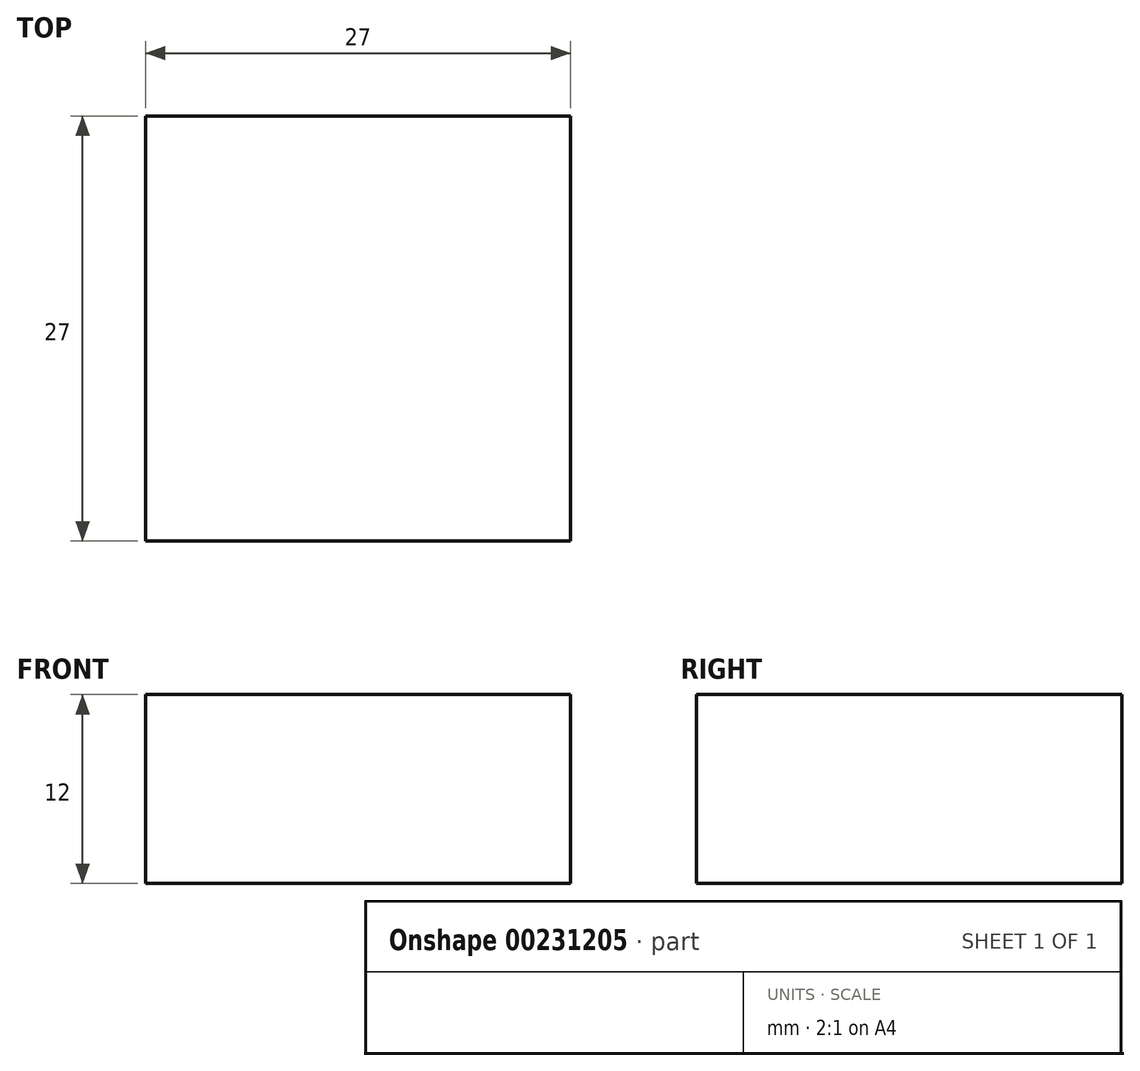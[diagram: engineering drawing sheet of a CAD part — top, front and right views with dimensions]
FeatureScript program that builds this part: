
annotation { "Feature Type Name" : "Feature", "Feature Type Description" : "" }
export const myFeature = defineFeature(function(context is Context, id is Id, definition is map)
    precondition{}
    {
        {
            assignVariable(context, id + "F0", {"name" : "foot_servo_width", "anyValue" : 12});
        }
        {
            var Q0;
            Q0=qCreatedBy(makeId("Top.planeOp"),FACE);
            var sketch = newSketch(context, id + "F1", { "sketchPlane" : qUnion([Q0])});
            skLineSegment(sketch, "E0.bottom", {"start": v(-35.31, -13.5) * mm, "end": v(-8.31, -13.5) * mm});
            skLineSegment(sketch, "E0.top", {"start": v(-35.31, 13.5) * mm, "end": v(-8.31, 13.5) * mm});
            skLineSegment(sketch, "E0.left", {"start": v(-35.31, -13.5) * mm, "end": v(-35.31, 13.5) * mm});
            skLineSegment(sketch, "E0.right", {"start": v(-8.31, -13.5) * mm, "end": v(-8.31, 13.5) * mm});
            skPoint(sketch, "E0.middle", {"position": v(-21.81, 0) * mm});
            skSolve(sketch);
        }
        {
            var Q0;
            Q0=makeQuery(id+"F1.imprint","IMPRINT",FACE,{"disambiguationData":[TD([[makeQuery(id+"F1.imprint","IMPRINT",EDGE,{"derivedFrom":sQuery(id+"F1.wireOp",EDGE,"E0.bottom")}),1.0]])]});
            extrude(context, id + "F2", {"entities" : qUnion([Q0]), "depth" : (getVariable(context, 'foot_servo_width') + 1.5) * mm, "hasSecondDirection" : true, "secondDirectionOppositeDirection" : false, "secondDirectionDepth" : 1.5 * mm});
        }
    });
